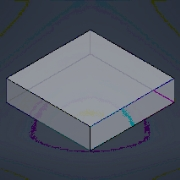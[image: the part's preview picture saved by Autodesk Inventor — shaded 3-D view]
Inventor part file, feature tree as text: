
AUTODESK INVENTOR PART (.ipt)
format: ipt  version: 2024.3 (Build 283343000, 343)  size: 135,168 bytes
history: native  units: mm
features: extrude x1, sketch x1
ambient origin geometry x8: Origin, YZ Plane, XZ Plane, XY Plane, X Axis, Y Axis, Z Axis, Center Point
bodies: Solid1 (feature_tree)
feature tree (2):
  extrude  "Extrusion1"  Depth=20.0mm
  sketch  "Sketch1"  dims[d0=35.0mm d1=20.0mm d2=20.0mm d3=0.0mm]
